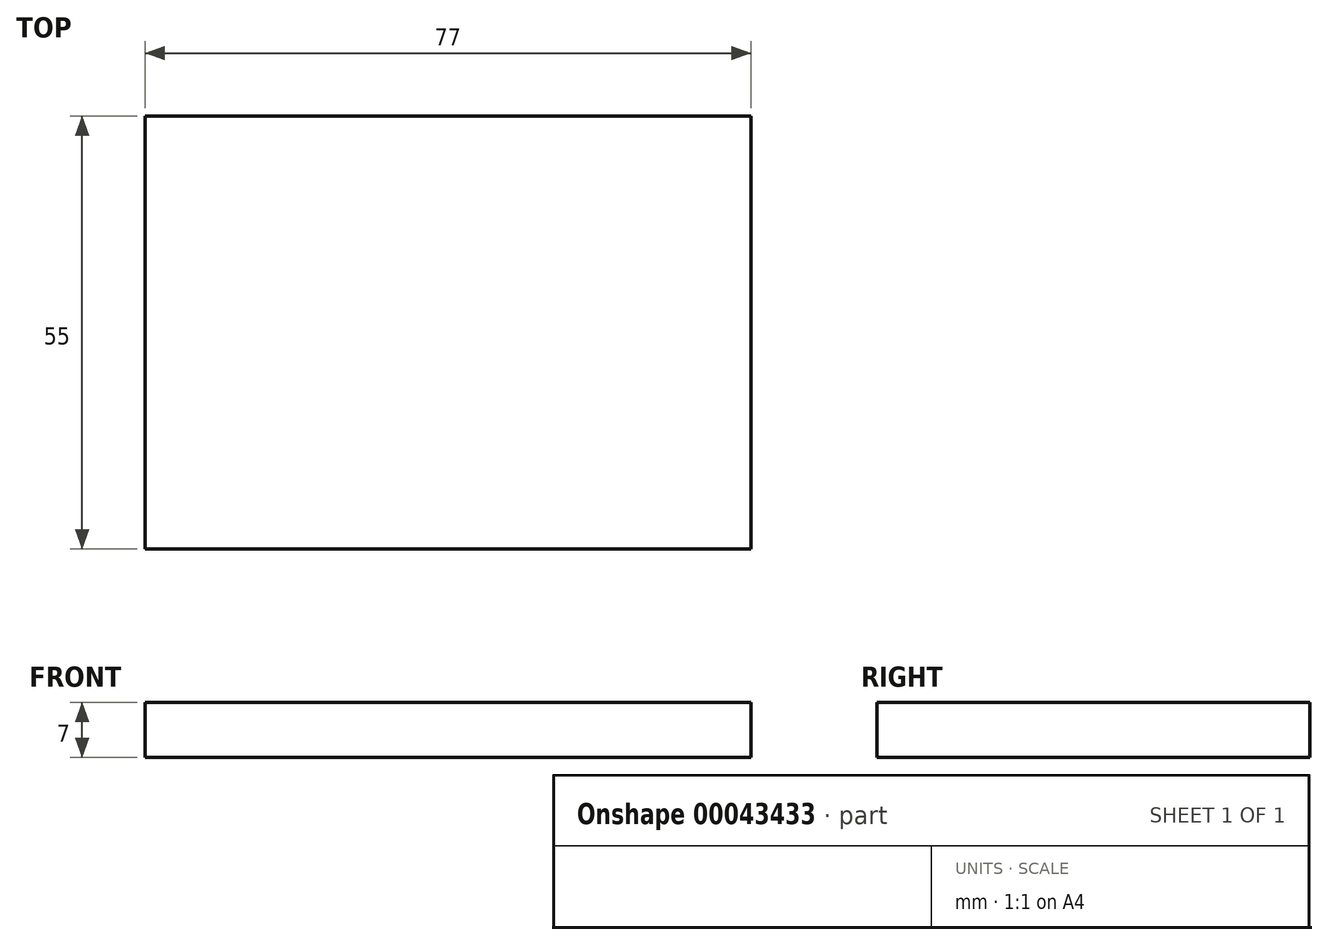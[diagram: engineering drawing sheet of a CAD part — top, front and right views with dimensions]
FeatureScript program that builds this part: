
annotation { "Feature Type Name" : "Feature", "Feature Type Description" : "" }
export const myFeature = defineFeature(function(context is Context, id is Id, definition is map)
    precondition{}
    {
        {
            var Q0;
            Q0=qCreatedBy(makeId("Top.planeOp"),FACE);
            var sketch = newSketch(context, id + "F0", { "sketchPlane" : qUnion([Q0])});
            skLineSegment(sketch, "E0.bottom", {"start": v(-26.47, 11.9) * mm, "end": v(50.53, 11.9) * mm});
            skLineSegment(sketch, "E0.top", {"start": v(-26.47, -43.1) * mm, "end": v(50.53, -43.1) * mm});
            skLineSegment(sketch, "E0.left", {"start": v(-26.47, 11.9) * mm, "end": v(-26.47, -43.1) * mm});
            skLineSegment(sketch, "E0.right", {"start": v(50.53, 11.9) * mm, "end": v(50.53, -43.1) * mm});
            skSolve(sketch);
        }
        {
            var Q0;
            Q0 = qSketchRegion(id + "F0", true);
            extrude(context, id + "F1", {"entities" : qUnion([Q0]), "depth" : 7 * mm});
        }
    });
